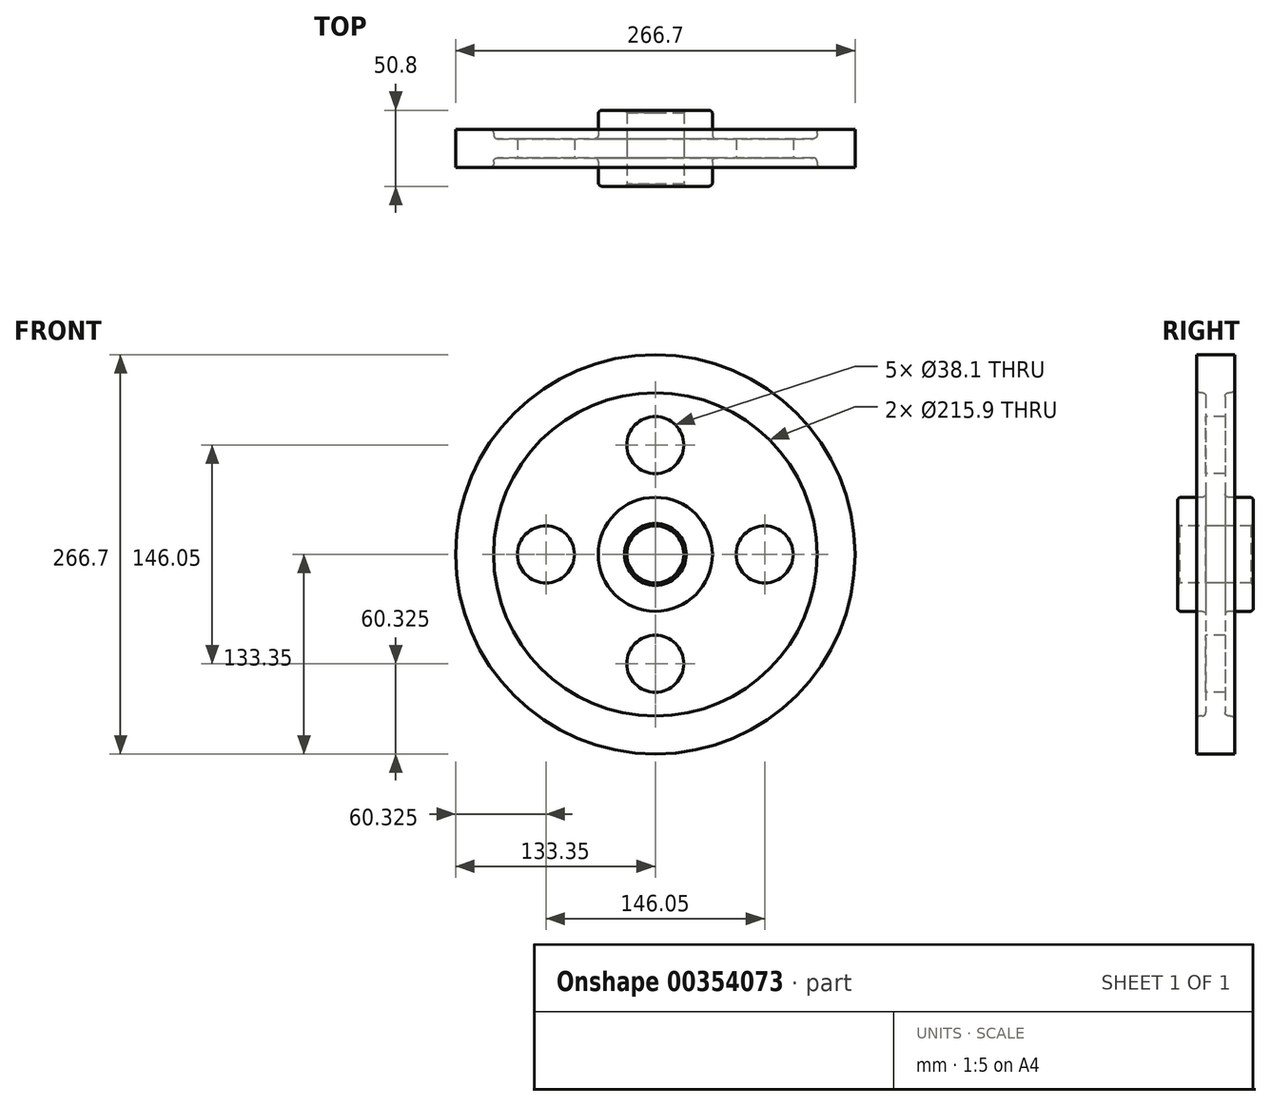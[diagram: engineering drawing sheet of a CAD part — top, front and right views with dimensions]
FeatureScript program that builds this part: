
annotation { "Feature Type Name" : "Feature", "Feature Type Description" : "" }
export const myFeature = defineFeature(function(context is Context, id is Id, definition is map)
    precondition{}
    {
        {
            var Q0;
            Q0=qCreatedBy(makeId("Right.planeOp"),FACE);
            var sketch = newSketch(context, id + "F0", { "sketchPlane" : qUnion([Q0])});
            skLineSegment(sketch, "E0", {"start": v(0, 0) * mm, "end": v(75.77, 0) * mm, "construction": true});
            skLineSegment(sketch, "E1.0", {"start": v(0, 19.05) * mm, "end": v(25.4, 19.05) * mm});
            skLineSegment(sketch, "E2.0", {"start": v(6.35, 38.1) * mm, "end": v(25.4, 38.1) * mm});
            skLineSegment(sketch, "E3.0", {"start": v(6.35, 107.95) * mm, "end": v(12.7, 107.95) * mm});
            skLineSegment(sketch, "E4.0", {"start": v(0, 133.35) * mm, "end": v(12.7, 133.35) * mm});
            skLineSegment(sketch, "E5", {"start": v(0, 38.1) * mm, "end": v(0, 0) * mm, "construction": true});
            skLineSegment(sketch, "E6.0", {"start": v(6.35, 107.95) * mm, "end": v(6.35, 38.1) * mm});
            skLineSegment(sketch, "E7.0", {"start": v(25.4, 38.1) * mm, "end": v(25.4, 19.05) * mm});
            skLineSegment(sketch, "E8.0", {"start": v(12.7, 133.35) * mm, "end": v(12.7, 107.95) * mm});
            skLineSegment(sketch, "E9.MirrorCS", {"start": v(-6.35, 107.95) * mm, "end": v(-6.35, 38.1) * mm});
            skLineSegment(sketch, "E10.MirrorCS", {"start": v(-6.35, 38.1) * mm, "end": v(-25.4, 38.1) * mm});
            skLineSegment(sketch, "E11.MirrorCS", {"start": v(-25.4, 38.1) * mm, "end": v(-25.4, 19.05) * mm});
            skLineSegment(sketch, "E12.MirrorCS", {"start": v(0, 19.05) * mm, "end": v(-25.4, 19.05) * mm});
            skLineSegment(sketch, "E13.MirrorCS", {"start": v(-12.7, 133.35) * mm, "end": v(-12.7, 107.95) * mm});
            skLineSegment(sketch, "E14.MirrorCS", {"start": v(0, 133.35) * mm, "end": v(-12.7, 133.35) * mm});
            skLineSegment(sketch, "E15", {"start": v(-12.7, 107.95) * mm, "end": v(-6.35, 107.95) * mm, "construction": true});
            skLineSegment(sketch, "E16", {"start": v(-12.7, 107.95) * mm, "end": v(-6.35, 107.95) * mm});
            skSolve(sketch);
        }
        {
            var Q0;
            Q0=makeQuery(id+"F0.imprint","IMPRINT",FACE,{"disambiguationData":[TD([[makeQuery(id+"F0.imprint","IMPRINT",EDGE,{"derivedFrom":sQuery(id+"F0.wireOp",EDGE,"E1.0")}),1.0]])]});
            var Q1;
            Q1=sQuery(id+"F0.wireOp",EDGE,"E0");
            revolve(context, id + "F1", {"entities" : qUnion([Q0]), "axis" : qUnion([Q1]), "revolveType" : RevolveType.FULL});
        }
        {
            var Q0;
            Q0=makeQuery(id+"F1.opRevolve","SWEPT_FACE",FACE,{"disambiguationData":[OSD([sQuery(id+"F0.wireOp",EDGE,"E9.MirrorCS")])]});
            var sketch = newSketch(context, id + "F2", { "sketchPlane" : qUnion([Q0])});
            skLineSegment(sketch, "E17", {"start": v(0, 0) * mm, "end": v(0, 73.03) * mm});
            skCircle(sketch, "E18", {"center": v(0, 73.03) * mm, "radius": 19.05 * mm});
            skCircle(sketch, "E19.1.0", {"center": v(-73.03, 0) * mm, "radius": 19.05 * mm});
            skCircle(sketch, "E19.2.0", {"center": v(0, -73.03) * mm, "radius": 19.05 * mm});
            skCircle(sketch, "E19.3.0", {"center": v(73.03, 0) * mm, "radius": 19.05 * mm});
            skPoint(sketch, "E19.center", {"position": v(0, 0) * mm});
            skSolve(sketch);
        }
        {
            var Q0;
            Q0=makeQuery(id+"F2.imprint","IMPRINT",FACE,{"disambiguationData":[TD([[makeQuery(id+"F2.imprint","IMPRINT",EDGE,{"derivedFrom":sQuery(id+"F2.wireOp",EDGE,"E19.3.0")}),1.0]])]});
            var Q1;
            Q1=makeQuery(id+"F2.imprint","IMPRINT",FACE,{"disambiguationData":[TD([[makeQuery(id+"F2.imprint","IMPRINT",EDGE,{"derivedFrom":sQuery(id+"F2.wireOp",EDGE,"E19.2.0")}),1.0]])]});
            var Q2;
            Q2=makeQuery(id+"F2.imprint","IMPRINT",FACE,{"disambiguationData":[TD([[makeQuery(id+"F2.imprint","IMPRINT",EDGE,{"derivedFrom":sQuery(id+"F2.wireOp",EDGE,"E19.1.0")}),1.0]])]});
            var Q3;
            Q3=makeQuery(id+"F2.imprint","IMPRINT",FACE,{"disambiguationData":[TD([[makeQuery(id+"F2.imprint","IMPRINT",EDGE,{"derivedFrom":sQuery(id+"F2.wireOp",EDGE,"E18")}),1.0]])]});
            extrude(context, id + "F3", {"entities" : qUnion([Q0, Q1, Q2, Q3]), "operationType" : NewBodyOperationType.REMOVE, "oppositeDirection" : true, "depth" : 25.4 * mm});
        }
        {
            var Q0;
            Q0=makeQuery(id+"F1.opRevolve","SWEPT_EDGE",EDGE,{"disambiguationData":[OSD([sQuery(id+"F0.wireOp",EDGE,"E13.MirrorCS"),sQuery(id+"F0.wireOp",EDGE,"E16")])]});
            var Q1;
            Q1=makeQuery(id+"F1.opRevolve","SWEPT_EDGE",EDGE,{"disambiguationData":[OSD([sQuery(id+"F0.wireOp",EDGE,"E9.MirrorCS"),sQuery(id+"F0.wireOp",EDGE,"E10.MirrorCS")])]});
            var Q2;
            Q2=makeQuery(id+"F1.opRevolve","SWEPT_EDGE",EDGE,{"disambiguationData":[OSD([sQuery(id+"F0.wireOp",EDGE,"E10.MirrorCS"),sQuery(id+"F0.wireOp",EDGE,"E11.MirrorCS")])]});
            var Q3;
            Q3=makeQuery(id+"F1.opRevolve","SWEPT_EDGE",EDGE,{"disambiguationData":[OSD([sQuery(id+"F0.wireOp",EDGE,"E9.MirrorCS"),sQuery(id+"F0.wireOp",EDGE,"E16")])]});
            var Q4;
            Q4=makeQuery(id+"F1.opRevolve","SWEPT_EDGE",EDGE,{"disambiguationData":[OSD([sQuery(id+"F0.wireOp",EDGE,"E3.0"),sQuery(id+"F0.wireOp",EDGE,"E6.0")])]});
            var Q5;
            Q5=makeQuery(id+"F1.opRevolve","SWEPT_EDGE",EDGE,{"disambiguationData":[OSD([sQuery(id+"F0.wireOp",EDGE,"E3.0"),sQuery(id+"F0.wireOp",EDGE,"E8.0")])]});
            var Q6;
            Q6=makeQuery(id+"F1.opRevolve","SWEPT_EDGE",EDGE,{"disambiguationData":[OSD([sQuery(id+"F0.wireOp",EDGE,"E2.0"),sQuery(id+"F0.wireOp",EDGE,"E6.0")])]});
            var Q7;
            Q7=makeQuery(id+"F1.opRevolve","SWEPT_EDGE",EDGE,{"disambiguationData":[OSD([sQuery(id+"F0.wireOp",EDGE,"E2.0"),sQuery(id+"F0.wireOp",EDGE,"E7.0")])]});
            fillet(context, id + "F4", {"entities" : qUnion([Q0, Q1, Q2, Q3, Q4, Q5, Q6, Q7]), "radius" : 2.54 * mm, "tangentPropagation" : true, "allowEdgeOverflow" : false});
        }
        {
            var Q0;
            Q0=makeQuery(id+"F1.opRevolve","SWEPT_EDGE",EDGE,{"disambiguationData":[OSD([sQuery(id+"F0.wireOp",EDGE,"E11.MirrorCS"),sQuery(id+"F0.wireOp",EDGE,"E12.MirrorCS")])]});
            var Q1;
            Q1=makeQuery(id+"F1.opRevolve","SWEPT_EDGE",EDGE,{"disambiguationData":[OSD([sQuery(id+"F0.wireOp",EDGE,"E1.0"),sQuery(id+"F0.wireOp",EDGE,"E7.0")])]});
            chamfer(context, id + "F5", {"entities" : qUnion([Q0, Q1]), "width" : 1.59 * mm, "tangentPropagation" : true});
        }
    });
